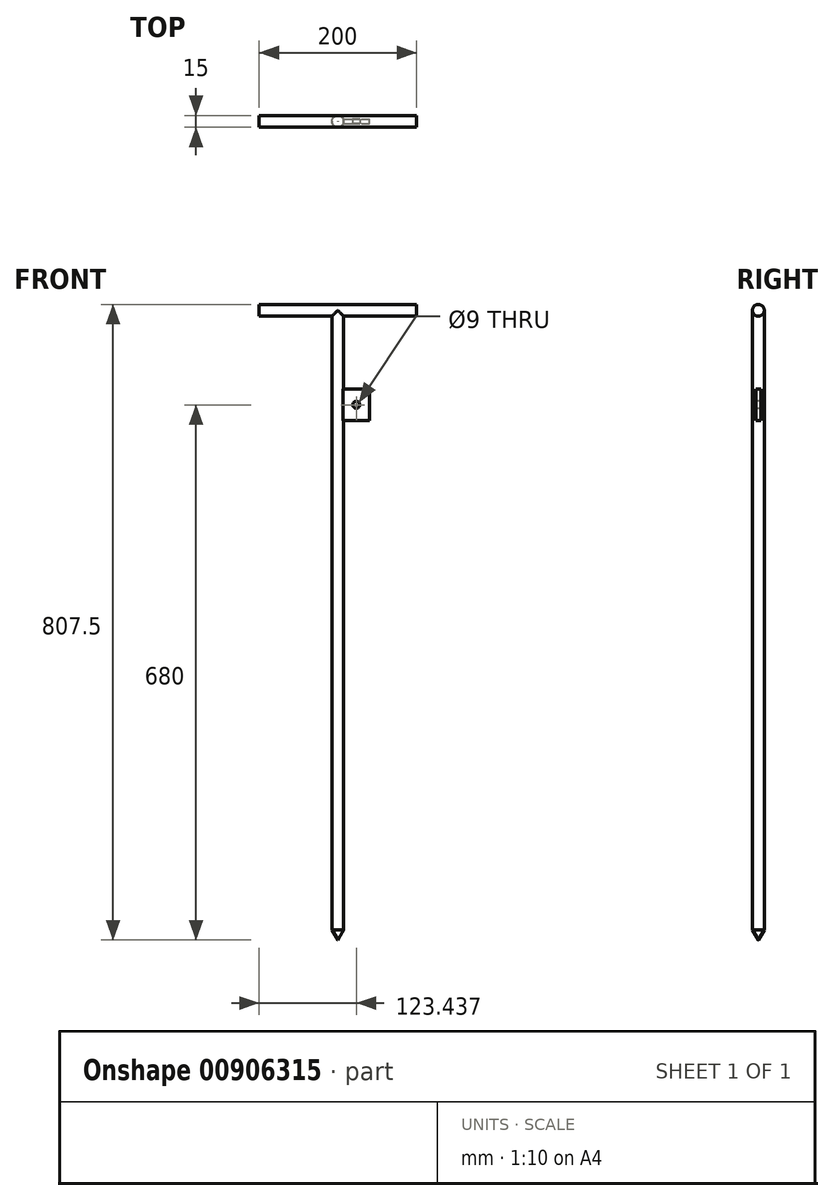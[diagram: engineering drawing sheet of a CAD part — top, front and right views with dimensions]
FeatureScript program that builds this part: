
annotation { "Feature Type Name" : "Feature", "Feature Type Description" : "" }
export const myFeature = defineFeature(function(context is Context, id is Id, definition is map)
    precondition{}
    {
        {
            var Q0;
            Q0=qCreatedBy(makeId("Top.planeOp"),FACE);
            var sketch = newSketch(context, id + "F0", { "sketchPlane" : qUnion([Q0])});
            skCircle(sketch, "E0", {"center": v(0, 0) * mm, "radius": 7.5 * mm});
            skSolve(sketch);
        }
        {
            var Q0;
            Q0 = qSketchRegion(id + "F0", true);
            extrude(context, id + "F1", {"entities" : qUnion([Q0]), "depth" : 800 * mm, "offsetDistance" : 25 * mm});
        }
        {
            var Q0;
            Q0=qCreatedBy(makeId("Right.planeOp"),FACE);
            var sketch = newSketch(context, id + "F2", { "sketchPlane" : qUnion([Q0])});
            skCircle(sketch, "E1", {"center": v(0, 800) * mm, "radius": 7.5 * mm});
            skSolve(sketch);
        }
        {
            var Q0;
            Q0 = qSketchRegion(id + "F2", true);
            extrude(context, id + "F3", {"entities" : qUnion([Q0]), "operationType" : NewBodyOperationType.ADD, "endBound" : BoundingType.SYMMETRIC, "depth" : 200 * mm, "offsetDistance" : 25 * mm});
        }
        {
            var Q0;
            Q0=qCreatedBy(makeId("Front.planeOp"),FACE);
            var sketch = newSketch(context, id + "F4", { "sketchPlane" : qUnion([Q0])});
            skLineSegment(sketch, "E2.bottom", {"start": v(0, 700) * mm, "end": v(40, 700) * mm});
            skLineSegment(sketch, "E2.top", {"start": v(0, 660) * mm, "end": v(40, 660) * mm});
            skLineSegment(sketch, "E2.left", {"start": v(0, 700) * mm, "end": v(0, 660) * mm});
            skLineSegment(sketch, "E2.right", {"start": v(40, 700) * mm, "end": v(40, 660) * mm});
            skSolve(sketch);
        }
        {
            var Q0;
            Q0 = qSketchRegion(id + "F4", true);
            extrude(context, id + "F5", {"entities" : qUnion([Q0]), "operationType" : NewBodyOperationType.ADD, "endBound" : BoundingType.SYMMETRIC, "depth" : 6 * mm, "offsetDistance" : 25 * mm});
        }
        {
            var Q0;
            Q0=makeQuery(id+"F5.opExtrude","CAP_FACE",FACE,{"disambiguationData":[OSD([sQuery(id+"F4.wireOp",EDGE,"E2.bottom"),sQuery(id+"F4.wireOp",EDGE,"E2.top"),sQuery(id+"F4.wireOp",EDGE,"E2.left"),sQuery(id+"F4.wireOp",EDGE,"E2.right")])],"isStart":false});
            var sketch = newSketch(context, id + "F6", { "sketchPlane" : qUnion([Q0])});
            skPoint(sketch, "E3", {"position": v(23.44, 680) * mm});
            skSolve(sketch);
        }
        {
            var Q0;
            Q0=sQuery(id+"F6.wireOp",VERTEX,"E3");
            var Q1;
            Q1=makeQuery(id+"F1.opExtrude","SWEPT_BODY",BODY,{"disambiguationData":[OSD([sQuery(id+"F0.wireOp",EDGE,"E0")])]});
            hole(context, id + "F7", {"style" : HoleStyle.SIMPLE, "endStyle" : HoleEndStyle.THROUGH, "standardTappedOrClearance" : lookupTablePath({ "fit" : "Normal", "standard" : "ISO", "size" : "M8", "type" : "Clearance" }), "standardBlindInLast" : lookupTablePath({ "fit" : "Normal", "standard" : "ISO", "size" : "M8", "type" : "Clearance" }), "holeDiameter" : 9 * mm, "majorDiameter" : 5 * mm, "isTappedThrough" : true, "tappedDepth" : 12 * mm, "tapClearance" : 3, "locations" : qUnion([Q0]), "scope" : qUnion([Q1])});
        }
        {
            var Q0;
            Q0=qCreatedBy(makeId("Front.planeOp"),FACE);
            var sketch = newSketch(context, id + "F8", { "sketchPlane" : qUnion([Q0])});
            skLineSegment(sketch, "E4", {"start": v(0, -0.1) * mm, "end": v(10, 17.22) * mm});
            skLineSegment(sketch, "E5", {"start": v(10, 17.22) * mm, "end": v(10, -0.1) * mm});
            skLineSegment(sketch, "E6", {"start": v(0, -0.1) * mm, "end": v(10, -0.1) * mm});
            skLineSegment(sketch, "E7", {"start": v(0, -0.1) * mm, "end": v(0, 9.9) * mm, "construction": true});
            skLineSegment(sketch, "E8", {"start": v(0.06, 0) * mm, "end": v(0.06, -0.1) * mm});
            skSolve(sketch);
        }
        {
            var Q0;
            {var subQ0=sQuery(id+"F8.wireOp",EDGE,"E5");Q0=makeQuery(id+"F8.imprint","IMPRINT",FACE,{"disambiguationData":[TD([[makeQuery(id+"F8.imprint","IMPRINT",EDGE,{"derivedFrom":subQ0}),-1.0]])]});}
            var Q1;
            Q1=sQuery(id+"F8.wireOp",EDGE,"E7");
            revolve(context, id + "F9", {"operationType" : NewBodyOperationType.REMOVE, "surfaceOperationType" : NewSurfaceOperationType.NEW, "entities" : qUnion([Q0]), "axis" : qUnion([Q1]), "revolveType" : RevolveType.FULL});
        }
    });
